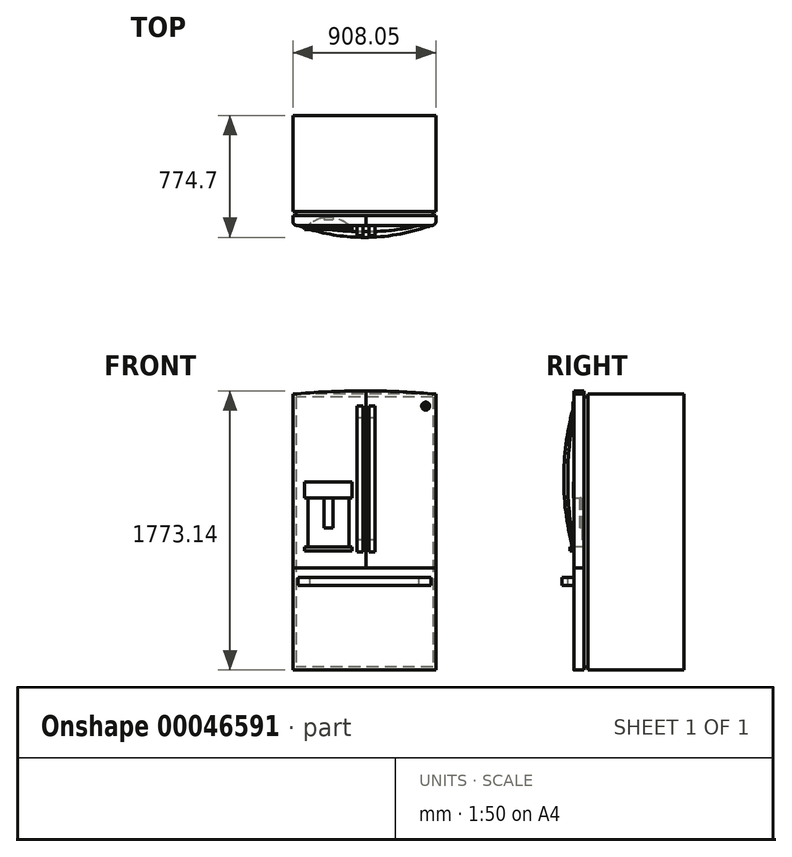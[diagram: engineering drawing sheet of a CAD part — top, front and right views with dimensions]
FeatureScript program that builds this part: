
annotation { "Feature Type Name" : "Feature", "Feature Type Description" : "" }
export const myFeature = defineFeature(function(context is Context, id is Id, definition is map)
    precondition{}
    {
        {
            var Q0;
            Q0=qCreatedBy(makeId("Front.planeOp"),FACE);
            var sketch = newSketch(context, id + "F0", { "sketchPlane" : qUnion([Q0])});
            skLineSegment(sketch, "E0.bottom", {"start": v(-463.95, 1156.1) * mm, "end": v(444.1, 1156.1) * mm, "construction": true});
            skLineSegment(sketch, "E0.top", {"start": v(-463.95, -596.5) * mm, "end": v(444.1, -596.5) * mm});
            skLineSegment(sketch, "E0.left", {"start": v(-463.95, 1156.1) * mm, "end": v(-463.95, -596.5) * mm});
            skLineSegment(sketch, "E0.right", {"start": v(444.1, 1156.1) * mm, "end": v(444.1, -596.5) * mm});
            skLineSegment(sketch, "E1", {"start": v(-463.95, 51.2) * mm, "end": v(444.1, 51.2) * mm});
            skLineSegment(sketch, "E2.bottom", {"start": v(-368.7, 496.57) * mm, "end": v(-108.35, 496.57) * mm});
            skLineSegment(sketch, "E2.top", {"start": v(-368.7, 186.46) * mm, "end": v(-108.35, 186.46) * mm});
            skLineSegment(sketch, "E2.left", {"start": v(-368.7, 496.57) * mm, "end": v(-368.7, 186.46) * mm});
            skLineSegment(sketch, "E2.right", {"start": v(-108.35, 496.57) * mm, "end": v(-108.35, 186.46) * mm});
            skLineSegment(sketch, "E3.bottom", {"start": v(-267.1, 306.07) * mm, "end": v(-209.95, 306.07) * mm});
            skLineSegment(sketch, "E3.top", {"start": v(-267.1, 496.57) * mm, "end": v(-209.95, 496.57) * mm});
            skLineSegment(sketch, "E3.left", {"start": v(-267.1, 306.07) * mm, "end": v(-267.1, 496.57) * mm});
            skLineSegment(sketch, "E3.right", {"start": v(-209.95, 306.07) * mm, "end": v(-209.95, 496.57) * mm});
            skLineSegment(sketch, "E4.bottom", {"start": v(-389.9, 598.17) * mm, "end": v(-87.14, 598.17) * mm});
            skLineSegment(sketch, "E4.top", {"start": v(-389.9, 496.57) * mm, "end": v(-87.14, 496.57) * mm});
            skLineSegment(sketch, "E4.left", {"start": v(-389.9, 598.17) * mm, "end": v(-389.9, 496.57) * mm});
            skLineSegment(sketch, "E4.right", {"start": v(-87.14, 598.17) * mm, "end": v(-87.14, 496.57) * mm});
            skLineSegment(sketch, "E5.bottom", {"start": v(-389.9, 161.06) * mm, "end": v(-87.14, 161.06) * mm});
            skLineSegment(sketch, "E5.top", {"start": v(-389.9, 186.46) * mm, "end": v(-87.14, 186.46) * mm});
            skLineSegment(sketch, "E5.left", {"start": v(-389.9, 161.06) * mm, "end": v(-389.9, 186.46) * mm});
            skLineSegment(sketch, "E5.right", {"start": v(-87.14, 161.06) * mm, "end": v(-87.14, 186.46) * mm});
            skArc(sketch, "E6", {"start": v(444.1, 1156.1) * mm, "mid": v(-9.92, 1176.64) * mm, "end": v(-463.95, 1156.1) * mm});
            skLineSegment(sketch, "E7", {"start": v(0, 51.2) * mm, "end": v(0, 1176.63) * mm});
            skSolve(sketch);
        }
        {
            var Q0;
            {var subQ4=sQuery(id+"F0.wireOp",EDGE,"E0.top");Q0=makeQuery(id+"F0.imprint","IMPRINT",FACE,{"disambiguationData":[TD([[makeQuery(id+"F0.imprint","IMPRINT",EDGE,{"derivedFrom":subQ4}),1.0]])]});}
            extrude(context, id + "F1", {"entities" : qUnion([Q0]), "oppositeDirection" : true, "depth" : 63.5 * mm});
        }
        {
            var Q0;
            Q0=makeQuery(id+"F0.imprint","IMPRINT",FACE,{"disambiguationData":[TD([[makeQuery(id+"F0.imprint","IMPRINT",EDGE,{"derivedFrom":sQuery(id+"F0.wireOp",EDGE,"E5.bottom")}),1.0]])]});
            var Q1;
            {var subQ4=sQuery(id+"F0.wireOp",EDGE,"E2.left");Q1=makeQuery(id+"F0.imprint","IMPRINT",FACE,{"disambiguationData":[TD([[makeQuery(id+"F0.imprint","IMPRINT",EDGE,{"derivedFrom":subQ4}),1.0]])]});}
            var Q2;
            Q2=makeQuery(id+"F0.imprint","IMPRINT",FACE,{"disambiguationData":[TD([[makeQuery(id+"F0.imprint","IMPRINT",EDGE,{"derivedFrom":sQuery(id+"F0.wireOp",EDGE,"E3.bottom")}),1.0]])]});
            var Q3;
            {var subQ5=sQuery(id+"F0.wireOp",EDGE,"E2.left");Q3=makeQuery(id+"F0.imprint","IMPRINT",FACE,{"disambiguationData":[TD([[makeQuery(id+"F0.imprint","IMPRINT",EDGE,{"derivedFrom":subQ5}),-1.0]])]});}
            var Q4;
            Q4=makeQuery(id+"F0.imprint","IMPRINT",FACE,{"disambiguationData":[TD([[makeQuery(id+"F0.imprint","IMPRINT",EDGE,{"derivedFrom":sQuery(id+"F0.wireOp",EDGE,"E4.bottom")}),-1.0]])]});
            extrude(context, id + "F2", {"entities" : qUnion([Q0, Q1, Q2, Q3, Q4]), "oppositeDirection" : true, "depth" : 63.5 * mm});
        }
        {
            var Q0;
            {var subQ0=sQuery(id+"F0.wireOp",EDGE,"E7");Q0=makeQuery(id+"F0.imprint","IMPRINT",FACE,{"disambiguationData":[TD([[makeQuery(id+"F0.imprint","IMPRINT",EDGE,{"derivedFrom":subQ0}),-1.0]])]});}
            extrude(context, id + "F3", {"entities" : qUnion([Q0]), "oppositeDirection" : true, "depth" : 63.5 * mm});
        }
        {
            var Q0;
            Q0=makeQuery(id+"F3.opExtrude","CAP_FACE",FACE,{"disambiguationData":[OSD([sQuery(id+"F0.wireOp",EDGE,"E0.right"),sQuery(id+"F0.wireOp",EDGE,"E1"),sQuery(id+"F0.wireOp",EDGE,"E6"),sQuery(id+"F0.wireOp",EDGE,"E7")])],"isStart":false});
            var sketch = newSketch(context, id + "F4", { "sketchPlane" : qUnion([Q0])});
            skLineSegment(sketch, "E8.bottom", {"start": v(-425.05, 1137.05) * mm, "end": v(444.9, 1137.05) * mm});
            skLineSegment(sketch, "E8.top", {"start": v(-425.05, -577.45) * mm, "end": v(444.9, -577.45) * mm});
            skLineSegment(sketch, "E8.left", {"start": v(-425.05, 1137.05) * mm, "end": v(-425.05, -577.45) * mm});
            skLineSegment(sketch, "E8.right", {"start": v(444.9, 1137.05) * mm, "end": v(444.9, -577.45) * mm});
            skSolve(sketch);
        }
        {
            var Q0;
            Q0=qSketchRegion(id+"F4",true);
            extrude(context, id + "F5", {"entities" : qUnion([Q0]), "depth" : 25.4 * mm});
        }
        {
            var Q0;
            Q0=makeQuery(id+"F5.opExtrude","CAP_FACE",FACE,{"disambiguationData":[OSD([sQuery(id+"F4.wireOp",EDGE,"E8.bottom"),sQuery(id+"F4.wireOp",EDGE,"E8.top"),sQuery(id+"F4.wireOp",EDGE,"E8.left"),sQuery(id+"F4.wireOp",EDGE,"E8.right")])],"isStart":false});
            var sketch = newSketch(context, id + "F6", { "sketchPlane" : qUnion([Q0])});
            skLineSegment(sketch, "E9.bottom", {"start": v(-444.1, 1156.1) * mm, "end": v(463.95, 1156.1) * mm});
            skLineSegment(sketch, "E9.top", {"start": v(-444.1, -596.5) * mm, "end": v(463.95, -596.5) * mm});
            skLineSegment(sketch, "E9.left", {"start": v(-444.1, 1156.1) * mm, "end": v(-444.1, -596.5) * mm});
            skLineSegment(sketch, "E9.right", {"start": v(463.95, 1156.1) * mm, "end": v(463.95, -596.5) * mm});
            skSolve(sketch);
        }
        {
            var Q0;
            Q0=qSketchRegion(id+"F6",true);
            extrude(context, id + "F7", {"entities" : qUnion([Q0]), "depth" : 609.6 * mm});
        }
        {
            var Q0;
            {var subQ4=sQuery(id+"F0.wireOp",EDGE,"E2.left");Q0=makeQuery(id+"F0.imprint","IMPRINT",FACE,{"disambiguationData":[TD([[makeQuery(id+"F0.imprint","IMPRINT",EDGE,{"derivedFrom":subQ4}),1.0]])]});}
            var Q1;
            Q1=makeQuery(id+"F0.imprint","IMPRINT",FACE,{"disambiguationData":[TD([[makeQuery(id+"F0.imprint","IMPRINT",EDGE,{"derivedFrom":sQuery(id+"F0.wireOp",EDGE,"E3.bottom")}),1.0]])]});
            extrude(context, id + "F8", {"entities" : qUnion([Q0, Q1]), "operationType" : NewBodyOperationType.REMOVE, "oppositeDirection" : true, "depth" : 50.8 * mm});
        }
        {
            var Q0;
            Q0=makeQuery(id+"F8.boolean.opBoolean","COPY",EDGE,{"derivedFrom":makeQuery(id+"F8.opExtrude","CAP_EDGE",EDGE,{"disambiguationData":[OSD([sQuery(id+"F0.wireOp",EDGE,"E2.right")])],"isStart":false})});
            var Q1;
            Q1=makeQuery(id+"F8.boolean.opBoolean","COPY",EDGE,{"derivedFrom":makeQuery(id+"F8.opExtrude","CAP_EDGE",EDGE,{"disambiguationData":[OSD([sQuery(id+"F0.wireOp",EDGE,"E2.left")])],"isStart":false})});
            fillet(context, id + "F9", {"entities" : qUnion([Q0, Q1]), "radius" : 190.5 * mm, "tangentPropagation" : true, "allowEdgeOverflow" : false});
        }
        {
            var Q0;
            Q0=makeQuery(id+"F0.imprint","IMPRINT",FACE,{"disambiguationData":[TD([[makeQuery(id+"F0.imprint","IMPRINT",EDGE,{"derivedFrom":sQuery(id+"F0.wireOp",EDGE,"E5.bottom")}),1.0]])]});
            extrude(context, id + "F10", {"entities" : qUnion([Q0]), "operationType" : NewBodyOperationType.ADD, "depth" : 25.4 * mm});
        }
        {
            var Q0;
            Q0=makeQuery(id+"F0.imprint","IMPRINT",FACE,{"disambiguationData":[TD([[makeQuery(id+"F0.imprint","IMPRINT",EDGE,{"derivedFrom":sQuery(id+"F0.wireOp",EDGE,"E4.bottom")}),-1.0]])]});
            extrude(context, id + "F11", {"entities" : qUnion([Q0]), "operationType" : NewBodyOperationType.ADD, "depth" : 3.17 * mm});
        }
        {
            var Q0;
            Q0=makeQuery(id+"F0.imprint","IMPRINT",FACE,{"disambiguationData":[TD([[makeQuery(id+"F0.imprint","IMPRINT",EDGE,{"derivedFrom":sQuery(id+"F0.wireOp",EDGE,"E3.bottom")}),1.0]])]});
            extrude(context, id + "F12", {"entities" : qUnion([Q0]), "operationType" : NewBodyOperationType.ADD, "endBound" : BoundingType.UP_TO_NEXT, "oppositeDirection" : true, "depth" : 12.7 * mm});
        }
        {
            var Q0;
            Q0=makeQuery(id+"F12.opExtrude","CAP_FACE",FACE,{"disambiguationData":[OSD([sQuery(id+"F0.wireOp",EDGE,"E3.bottom"),sQuery(id+"F0.wireOp",EDGE,"E3.left"),sQuery(id+"F0.wireOp",EDGE,"E3.right"),sQuery(id+"F0.wireOp",EDGE,"E4.top")])],"isStart":true});
            extrude(context, id + "F13", {"entities" : qUnion([Q0]), "operationType" : NewBodyOperationType.REMOVE, "oppositeDirection" : true, "depth" : 38.1 * mm});
        }
        {
            var Q0;
            {var subQ0=sQuery(id+"F0.wireOp",EDGE,"E7");Q0=makeQuery(id+"F0.imprint","IMPRINT",FACE,{"disambiguationData":[TD([[makeQuery(id+"F0.imprint","IMPRINT",EDGE,{"derivedFrom":subQ0}),-1.0]])]});}
            var sketch = newSketch(context, id + "F14", { "sketchPlane" : qUnion([Q0])});
            skLineSegment(sketch, "E10.bottom", {"start": v(-432.2, -8.49) * mm, "end": v(412.35, -8.49) * mm});
            skLineSegment(sketch, "E10.top", {"start": v(-432.2, -59.29) * mm, "end": v(412.35, -59.29) * mm});
            skLineSegment(sketch, "E10.left", {"start": v(-432.2, -8.49) * mm, "end": v(-432.2, -59.29) * mm});
            skLineSegment(sketch, "E10.right", {"start": v(412.35, -8.49) * mm, "end": v(412.35, -59.29) * mm});
            skLineSegment(sketch, "E11.bottom", {"start": v(57.15, 1079.9) * mm, "end": v(19.05, 1079.9) * mm});
            skLineSegment(sketch, "E11.top", {"start": v(57.15, 152.8) * mm, "end": v(19.05, 152.8) * mm});
            skLineSegment(sketch, "E11.left", {"start": v(57.15, 1079.9) * mm, "end": v(57.15, 152.8) * mm});
            skLineSegment(sketch, "E11.right", {"start": v(19.05, 1079.9) * mm, "end": v(19.05, 152.8) * mm});
            skLineSegment(sketch, "E12.bottom", {"start": v(-19.05, 152.8) * mm, "end": v(-57.15, 152.8) * mm});
            skLineSegment(sketch, "E12.top", {"start": v(-19.05, 1079.9) * mm, "end": v(-57.15, 1079.9) * mm});
            skLineSegment(sketch, "E12.left", {"start": v(-19.05, 152.8) * mm, "end": v(-19.05, 1079.9) * mm});
            skLineSegment(sketch, "E12.right", {"start": v(-57.15, 152.8) * mm, "end": v(-57.15, 1079.9) * mm});
            skSolve(sketch);
        }
        {
            var Q0;
            Q0=makeQuery(id+"F14.imprint","IMPRINT",FACE,{"disambiguationData":[TD([[makeQuery(id+"F14.imprint","IMPRINT",EDGE,{"derivedFrom":sQuery(id+"F14.wireOp",EDGE,"E10.bottom")}),-1.0]])]});
            extrude(context, id + "F15", {"entities" : qUnion([Q0]), "operationType" : NewBodyOperationType.ADD, "depth" : 76.2 * mm});
        }
        {
            var Q0;
            Q0=makeQuery(id+"F14.imprint","IMPRINT",FACE,{"disambiguationData":[TD([[makeQuery(id+"F14.imprint","IMPRINT",EDGE,{"derivedFrom":sQuery(id+"F14.wireOp",EDGE,"E11.bottom")}),1.0]])]});
            extrude(context, id + "F16", {"entities" : qUnion([Q0]), "operationType" : NewBodyOperationType.ADD, "depth" : 63.5 * mm});
        }
        {
            var Q0;
            Q0=makeQuery(id+"F14.imprint","IMPRINT",FACE,{"disambiguationData":[TD([[makeQuery(id+"F14.imprint","IMPRINT",EDGE,{"derivedFrom":sQuery(id+"F14.wireOp",EDGE,"E12.bottom")}),-1.0]])]});
            extrude(context, id + "F17", {"entities" : qUnion([Q0]), "operationType" : NewBodyOperationType.ADD, "depth" : 63.5 * mm});
        }
        {
            var Q0;
            Q0=makeQuery(id+"F15.opExtrude","SWEPT_FACE",FACE,{"disambiguationData":[OSD([sQuery(id+"F14.wireOp",EDGE,"E10.bottom")])]});
            var sketch = newSketch(context, id + "F18", { "sketchPlane" : qUnion([Q0])});
            skLineSegment(sketch, "E13.bottom", {"start": v(-356, 0) * mm, "end": v(336.15, 0) * mm});
            skLineSegment(sketch, "E13.top", {"start": v(-356, -38.1) * mm, "end": v(336.15, -38.1) * mm});
            skLineSegment(sketch, "E13.left", {"start": v(-356, 0) * mm, "end": v(-356, -38.1) * mm});
            skLineSegment(sketch, "E13.right", {"start": v(336.15, 0) * mm, "end": v(336.15, -38.1) * mm});
            skSolve(sketch);
        }
        {
            var Q0;
            Q0=qSketchRegion(id+"F18",true);
            extrude(context, id + "F19", {"entities" : qUnion([Q0]), "operationType" : NewBodyOperationType.REMOVE, "endBound" : BoundingType.THROUGH_ALL, "oppositeDirection" : true, "depth" : 25.4 * mm});
        }
        {
            var Q0;
            Q0=makeQuery(id+"F17.opExtrude","SWEPT_FACE",FACE,{"disambiguationData":[OSD([sQuery(id+"F14.wireOp",EDGE,"E12.right")])]});
            var sketch = newSketch(context, id + "F20", { "sketchPlane" : qUnion([Q0])});
            skLineSegment(sketch, "E14.bottom", {"start": v(0, 229) * mm, "end": v(38.1, 229) * mm});
            skLineSegment(sketch, "E14.top", {"start": v(0, 1003.7) * mm, "end": v(38.1, 1003.7) * mm});
            skLineSegment(sketch, "E14.left", {"start": v(0, 229) * mm, "end": v(0, 1003.7) * mm});
            skLineSegment(sketch, "E14.right", {"start": v(38.1, 229) * mm, "end": v(38.1, 1003.7) * mm});
            skSolve(sketch);
        }
        {
            var Q0;
            Q0 = qSketchRegion(id + "F20", true);
            extrude(context, id + "F21", {"entities" : qUnion([Q0]), "operationType" : NewBodyOperationType.REMOVE, "oppositeDirection" : true, "depth" : 304.8 * mm});
        }
        {
            var Q0;
            Q0=makeQuery(id+"F16.opExtrude","SWEPT_FACE",FACE,{"disambiguationData":[OSD([sQuery(id+"F14.wireOp",EDGE,"E11.left")])]});
            var sketch = newSketch(context, id + "F22", { "sketchPlane" : qUnion([Q0])});
            skLineSegment(sketch, "E15.bottom", {"start": v(-38.1, 229) * mm, "end": v(0, 229) * mm});
            skLineSegment(sketch, "E15.top", {"start": v(-38.1, 1003.7) * mm, "end": v(0, 1003.7) * mm});
            skLineSegment(sketch, "E15.left", {"start": v(-38.1, 229) * mm, "end": v(-38.1, 1003.7) * mm});
            skLineSegment(sketch, "E15.right", {"start": v(0, 229) * mm, "end": v(0, 1003.7) * mm});
            skSolve(sketch);
        }
        {
            var Q0;
            Q0=makeQuery(id+"F22.imprint","IMPRINT",FACE,{"disambiguationData":[TD([[makeQuery(id+"F22.imprint","IMPRINT",EDGE,{"derivedFrom":sQuery(id+"F22.wireOp",EDGE,"E15.bottom")}),1.0]])]});
            extrude(context, id + "F23", {"entities" : qUnion([Q0]), "operationType" : NewBodyOperationType.REMOVE, "oppositeDirection" : true, "depth" : 50.8 * mm});
        }
        {
            var Q0;
            Q0=makeQuery(id+"F23.boolean.opBoolean","COPY",EDGE,{"derivedFrom":makeQuery(id+"F23.opExtrude","SWEPT_EDGE",EDGE,{"disambiguationData":[OSD([sQuery(id+"F22.wireOp",EDGE,"E15.top"),sQuery(id+"F22.wireOp",EDGE,"E15.left")])]})});
            var Q1;
            Q1=makeQuery(id+"F23.boolean.opBoolean","COPY",EDGE,{"derivedFrom":makeQuery(id+"F23.opExtrude","SWEPT_EDGE",EDGE,{"disambiguationData":[OSD([sQuery(id+"F22.wireOp",EDGE,"E15.bottom"),sQuery(id+"F22.wireOp",EDGE,"E15.left")])]})});
            var Q2;
            Q2=makeQuery(id+"F21.boolean.opBoolean","COPY",EDGE,{"derivedFrom":makeQuery(id+"F21.opExtrude","SWEPT_EDGE",EDGE,{"disambiguationData":[OSD([sQuery(id+"F20.wireOp",EDGE,"E14.bottom"),sQuery(id+"F20.wireOp",EDGE,"E14.right")])]})});
            var Q3;
            Q3=makeQuery(id+"F16.opExtrude","CAP_EDGE",EDGE,{"disambiguationData":[OSD([sQuery(id+"F14.wireOp",EDGE,"E11.bottom")])],"isStart":false});
            var Q4;
            Q4=makeQuery(id+"F17.opExtrude","CAP_EDGE",EDGE,{"disambiguationData":[OSD([sQuery(id+"F14.wireOp",EDGE,"E12.top")])],"isStart":false});
            var Q5;
            Q5=makeQuery(id+"F16.opExtrude","CAP_EDGE",EDGE,{"disambiguationData":[OSD([sQuery(id+"F14.wireOp",EDGE,"E11.top")])],"isStart":false});
            var Q6;
            Q6=makeQuery(id+"F17.opExtrude","CAP_EDGE",EDGE,{"disambiguationData":[OSD([sQuery(id+"F14.wireOp",EDGE,"E12.bottom")])],"isStart":false});
            var Q7;
            Q7=makeQuery(id+"F21.boolean.opBoolean","COPY",EDGE,{"derivedFrom":makeQuery(id+"F21.opExtrude","SWEPT_EDGE",EDGE,{"disambiguationData":[OSD([sQuery(id+"F20.wireOp",EDGE,"E14.top"),sQuery(id+"F20.wireOp",EDGE,"E14.right")])]})});
            fillet(context, id + "F24", {"entities" : qUnion([Q0, Q1, Q2, Q3, Q4, Q5, Q6, Q7]), "radius" : 1723.4 * mm, "tangentPropagation" : true, "allowEdgeOverflow" : false});
        }
        {
            var Q0;
            Q0=makeQuery(id+"F15.opExtrude","CAP_EDGE",EDGE,{"disambiguationData":[OSD([sQuery(id+"F14.wireOp",EDGE,"E10.left")])],"isStart":false});
            var Q1;
            Q1=makeQuery(id+"F15.opExtrude","CAP_EDGE",EDGE,{"disambiguationData":[OSD([sQuery(id+"F14.wireOp",EDGE,"E10.right")])],"isStart":false});
            var Q2;
            Q2=makeQuery(id+"F19.boolean.opBoolean","COPY",EDGE,{"derivedFrom":makeQuery(id+"F19.opExtrude","SWEPT_EDGE",EDGE,{"disambiguationData":[OSD([sQuery(id+"F18.wireOp",EDGE,"E13.top"),sQuery(id+"F18.wireOp",EDGE,"E13.right")])]})});
            var Q3;
            Q3=makeQuery(id+"F19.boolean.opBoolean","COPY",EDGE,{"derivedFrom":makeQuery(id+"F19.opExtrude","SWEPT_EDGE",EDGE,{"disambiguationData":[OSD([sQuery(id+"F18.wireOp",EDGE,"E13.top"),sQuery(id+"F18.wireOp",EDGE,"E13.left")])]})});
            fillet(context, id + "F25", {"entities" : qUnion([Q0, Q1, Q2, Q3]), "radius" : 1206.5 * mm, "tangentPropagation" : true, "allowEdgeOverflow" : false});
        }
        {
            var Q0;
            Q0=makeQuery(id+"F23.boolean.opBoolean","MERGE",FACE,{"derivedFrom":[makeQuery(id+"F3.opExtrude","CAP_FACE",FACE,{"disambiguationData":[OSD([sQuery(id+"F0.wireOp",EDGE,"E0.right"),sQuery(id+"F0.wireOp",EDGE,"E1"),sQuery(id+"F0.wireOp",EDGE,"E6"),sQuery(id+"F0.wireOp",EDGE,"E7")])],"isStart":true}),makeQuery(id+"F23.opExtrude","SWEPT_FACE",FACE,{"disambiguationData":[OSD([sQuery(id+"F22.wireOp",EDGE,"E15.right")])]})]});
            var sketch = newSketch(context, id + "F26", { "sketchPlane" : qUnion([Q0])});
            skCircle(sketch, "E16", {"center": v(379.68, 1079.9) * mm, "radius": 25.4 * mm});
            skSolve(sketch);
        }
        {
            var Q0;
            Q0=makeQuery(id+"F26.imprint","IMPRINT",FACE,{"disambiguationData":[TD([[makeQuery(id+"F26.imprint","IMPRINT",EDGE,{"derivedFrom":sQuery(id+"F26.wireOp",EDGE,"E16")}),1.0]])]});
            var Q1;
            Q1=sQuery(id+"F26.wireOp",EDGE,"E16");
            extrude(context, id + "F27", {"entities" : qUnion([Q0]), "surfaceEntities" : qUnion([Q1]), "depth" : 6.35 * mm});
        }
        {
            var Q0;
            Q0=makeQuery(id+"F27.opExtrude","CAP_EDGE",EDGE,{"disambiguationData":[OSD([sQuery(id+"F26.wireOp",EDGE,"E16")])],"isStart":false});
            fillet(context, id + "F28", {"entities" : qUnion([Q0]), "radius" : 3.17 * mm, "tangentPropagation" : true, "allowEdgeOverflow" : false});
        }
        {
            var Q0;
            Q0=makeQuery(id+"F27.opExtrude","CAP_FACE",FACE,{"disambiguationData":[OSD([sQuery(id+"F26.wireOp",EDGE,"E16")])],"isStart":false});
            var sketch = newSketch(context, id + "F29", { "sketchPlane" : qUnion([Q0])});
            skText(sketch, "E17", { "text": "GE", "fontName": "NotoSerif-BoldItalic.ttf"});
            const initialGuessF29  = {"E17": [0.36155, 1.07014, 1, 0, 0.01871]};
            skSetInitialGuess(sketch, initialGuessF29);
            skSolve(sketch);
        }
        {
            var Q0;
            Q0 = qSketchRegion(id + "F29", true);
            extrude(context, id + "F30", {"entities" : qUnion([Q0]), "operationType" : NewBodyOperationType.REMOVE, "oppositeDirection" : true, "depth" : 3.17 * mm});
        }
        {
            var Q0;
            Q0=makeQuery(id+"F1.opExtrude","CAP_EDGE",EDGE,{"disambiguationData":[OSD([sQuery(id+"F0.wireOp",EDGE,"E0.right")])],"isStart":true});
            var Q1;
            Q1=makeQuery(id+"F3.opExtrude","CAP_EDGE",EDGE,{"disambiguationData":[OSD([sQuery(id+"F0.wireOp",EDGE,"E0.right")])],"isStart":true});
            var Q2;
            Q2=makeQuery(id+"F2.opExtrude","CAP_EDGE",EDGE,{"disambiguationData":[OSD([sQuery(id+"F0.wireOp",EDGE,"E0.left")])],"isStart":true});
            var Q3;
            Q3=makeQuery(id+"F1.opExtrude","CAP_EDGE",EDGE,{"disambiguationData":[OSD([sQuery(id+"F0.wireOp",EDGE,"E0.left")])],"isStart":true});
            fillet(context, id + "F31", {"entities" : qUnion([Q0, Q1, Q2, Q3]), "radius" : 25.4 * mm, "tangentPropagation" : true, "allowEdgeOverflow" : false});
        }
    });
